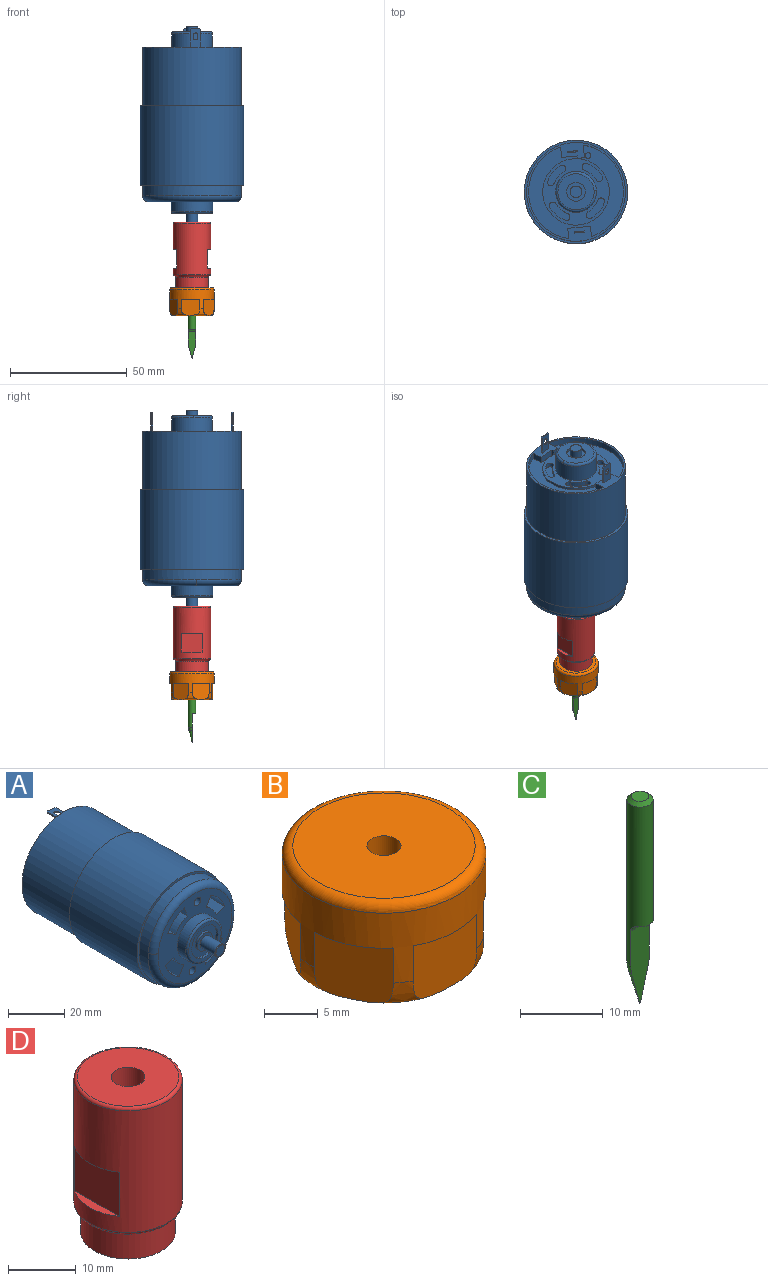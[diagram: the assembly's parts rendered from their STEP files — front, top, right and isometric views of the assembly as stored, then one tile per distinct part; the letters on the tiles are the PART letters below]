
ASSEMBLY  parts=4 mates=3
PART A: 110 faces, bbox 45.6x88x45.6 mm
  f0: torus R=18.65mm, axis (0,1,0), area 249.7mm2, adj f6,f28,f41
  f1: torus R=8.15mm, axis (0,1,0), area 31.9mm2, adj f8,f79,f85
  f2: torus R=7.75mm, axis (0,-1,0), area 41.4mm2, adj f19,f102,f104
  f3: torus R=2.25mm, axis (0,1,0), area 3mm2, adj f23,f107,f109
  f4: cylinder r=22.15mm len=44.3mm, axis (0,1,0), area 4731.9mm2, adj f25,f26
  f5: cylinder r=21.15mm len=42.3mm, axis (0,-1,0), area 3322.2mm2, adj f25,f27
  f6: cylinder r=21.15mm len=42.3mm, axis (0,-1,0), area 611.3mm2, adj f0,f26,f28
  f7: cylinder r=20.3mm len=39.26mm, axis (0,1,0), area 151mm2, adj f27,f31,f38,f51
  f8: cylinder r=8.9mm len=17.8mm, axis (0,-1,0), area 237.7mm2, adj f1,f41,f79
  f9: cylinder r=1.65mm len=11.5mm, axis (0,-1,0), area 119.2mm2, adj f13,f41
  f10: cylinder r=1.65mm len=11.5mm, axis (0,-1,0), area 119.2mm2, adj f14,f41
  f11: cylinder r=14.25mm len=28.5mm, axis (0,1,0), area 89.5mm2, adj f51,f83
  f12: cylinder r=1.25mm len=2.5mm, axis (0,1,0), area 0.8mm2, adj f51,f84
  f13: cone r=1.65mm half-angle=59deg, axis (0,-1,0), area 10mm2, adj f9
  f14: cone r=1.65mm half-angle=59deg, axis (0,-1,0), area 10mm2, adj f10
  f15: cylinder r=1.5mm len=2.9mm, axis (0,1,0), area 9.4mm2, adj f83,f86,f87,f98
  f16: cylinder r=1.5mm len=2.9mm, axis (0,1,0), area 9.4mm2, adj f83,f89,f90,f99
  f17: cylinder r=1.5mm len=2.79mm, axis (0,1,0), area 9.4mm2, adj f83,f92,f94,f100
  f18: cylinder r=1.5mm len=2.79mm, axis (0,1,0), area 9.4mm2, adj f83,f95,f97,f101
  f19: cylinder r=8.75mm len=17.5mm, axis (0,-1,0), area 412.3mm2, adj f2,f83,f102
  f20: cylinder r=6.62mm len=13.25mm, axis (0,-1,0), area 41.6mm2, adj f85,f103
  f21: cylinder r=3.75mm len=7.5mm, axis (0,-1,0), area 23.6mm2, adj f103,f105
  f22: cylinder r=4mm len=8mm, axis (0,1,0), area 25.1mm2, adj f104,f106
  f23: cylinder r=2.5mm len=7.55mm, axis (0,-1,0), area 118.6mm2, adj f3,f105,f107
  f24: cylinder r=2.5mm len=5mm, axis (0,-1,0), area 53.4mm2, adj f106,f108
  f25: plane 44.3x44.3mm, normal (0,1,0), area 136mm2, adj f4,f5
  f26: plane 44.3x44.3mm, normal (0,-1,0), area 136mm2, adj f4,f6
  f27: plane 42.3x42.3mm, normal (0,1,0), area 203.5mm2, adj f5,f7,f29,f30,f31,f32,f33,f34
  f28: torus R=18.65mm, axis (0,1,0), area 249.7mm2, adj f0,f6,f41
  f29: plane 8.15x4.58mm, normal (0.09,0,1), area 32.1mm2, adj f27,f42,f43,f44,f45,f46,f47,f48
  f30: plane 8.15x4.58mm, normal (-0.09,0,-1), area 32.1mm2, adj f27,f42,f43,f44,f45,f46,f47,f48
  f31: plane 4.44x2.8mm, normal (1,0,-0.09), area 12.5mm2, adj f7,f27,f32,f51
  f32: plane 9.71x2.8mm, normal (-0.09,0,-1), area 27.3mm2, adj f27,f31,f33,f51
  f33: plane 4.44x2.8mm, normal (-1,0,0.09), area 12.5mm2, adj f27,f32,f34,f51
  f34: cylinder r=20.3mm len=39.26mm, axis (0,1,0), area 151mm2, adj f27,f33,f35,f51
  f35: plane 4.44x2.8mm, normal (-1,0,0.09), area 12.5mm2, adj f27,f34,f36,f51
  f36: plane 6.92x2.8mm, normal (0.09,0,1), area 19.4mm2, adj f27,f35,f51,f52
  f37: plane 2.8x2.8mm, normal (0.09,0,1), area 7.9mm2, adj f27,f38,f51,f52
  f38: plane 5.44x2.8mm, normal (1,0,-0.09), area 15.3mm2, adj f7,f27,f37,f51
  f39: plane 8.15x4.58mm, normal (-0.09,0,-1), area 32.1mm2, adj f27,f53,f54,f55,f56,f57,f58,f59
  f40: plane 8.15x4.58mm, normal (0.09,0,1), area 32.1mm2, adj f27,f53,f54,f55,f56,f57,f58,f59
  f41: plane 37.3x37.3mm, normal (0,-1,0), area 647.6mm2, adj f0,f8,f9,f10,f28,f62,f63,f64
  f42: plane 3.63x0.81mm, normal (0,1,0), area 1.8mm2, adj f29,f30,f43,f46
  f43: plane 0.54x0.54mm, normal (-0.7,0.71,0.06), area 0.4mm2, adj f29,f30,f42,f44
  f44: plane 7.65x0.5mm, normal (-1,0,0.09), area 3.8mm2, adj f27,f29,f30,f43
  f45: plane 7.65x0.5mm, normal (1,0,-0.09), area 3.8mm2, adj f27,f29,f30,f46
  f46: plane 0.54x0.54mm, normal (0.7,0.71,-0.06), area 0.4mm2, adj f29,f30,f42,f45
  f47: plane 1x0.5mm, normal (1,0,-0.09), area 0.5mm2, adj f29,f30,f48,f50
  f48: cylinder r=1mm len=2.04mm, axis (0.09,0,1), area 1.6mm2, adj f29,f30,f47,f49
  f49: plane 1x0.5mm, normal (-1,0,0.09), area 0.5mm2, adj f29,f30,f48,f50
  f50: cylinder r=1mm len=2.04mm, axis (0.09,0,1), area 1.6mm2, adj f29,f30,f47,f49
  f51: plane 40.6x40.11mm, normal (0,1,0), area 554.3mm2, adj f7,f11,f12,f31,f32,f33,f34,f35
  f52: plane 2.8x1mm, normal (-1,0,0.09), area 2.8mm2, adj f27,f36,f37,f51
  f53: plane 7.65x0.5mm, normal (-1,0,0.09), area 3.8mm2, adj f27,f39,f40,f54
  f54: plane 0.54x0.54mm, normal (-0.7,0.71,0.06), area 0.4mm2, adj f39,f40,f53,f55
  f55: plane 3.63x0.81mm, normal (0,1,0), area 1.8mm2, adj f39,f40,f54,f56
  f56: plane 0.54x0.54mm, normal (0.7,0.71,-0.06), area 0.4mm2, adj f39,f40,f55,f57
  f57: plane 7.65x0.5mm, normal (1,0,-0.09), area 3.8mm2, adj f27,f39,f40,f56
  f58: plane 1x0.5mm, normal (-1,0,0.09), area 0.5mm2, adj f39,f40,f59,f61
  f59: cylinder r=1mm len=2.04mm, axis (-0.09,0,-1), area 1.6mm2, adj f39,f40,f58,f60
  f60: plane 1x0.5mm, normal (1,0,-0.09), area 0.5mm2, adj f39,f40,f59,f61
  f61: cylinder r=1mm len=2.04mm, axis (-0.09,0,-1), area 1.6mm2, adj f39,f40,f58,f60
  f62: plane 10x4.42mm, normal (-0.94,0,-0.34), area 47mm2, adj f41,f63,f65,f78
  f63: cylinder r=11.3mm len=10mm, axis (0,-1,0), area 78.9mm2, adj f41,f62,f64,f78
  f64: plane 10x4.07mm, normal (0.5,0,0.87), area 47mm2, adj f41,f63,f65,f78
  f65: cylinder r=16mm len=10mm, axis (0,-1,0), area 111.7mm2, adj f41,f62,f64,f78
  f66: cylinder r=16mm len=10mm, axis (0,-1,0), area 111.7mm2, adj f41,f67,f69,f80
  f67: plane 10x4.42mm, normal (0.94,0,0.34), area 47mm2, adj f41,f66,f68,f80
  f68: cylinder r=11.3mm len=10mm, axis (0,-1,0), area 78.9mm2, adj f41,f67,f69,f80
  f69: plane 10x4.07mm, normal (-0.5,0,-0.87), area 47mm2, adj f41,f66,f68,f80
  f70: plane 10x4.42mm, normal (-0.34,0,0.94), area 47mm2, adj f41,f71,f73,f81
  f71: cylinder r=11.3mm len=10mm, axis (0,-1,0), area 78.9mm2, adj f41,f70,f72,f81
  f72: plane 10x4.07mm, normal (0.87,0,-0.5), area 47mm2, adj f41,f71,f73,f81
  f73: cylinder r=16mm len=10mm, axis (0,-1,0), area 111.7mm2, adj f41,f70,f72,f81
  f74: cylinder r=16mm len=10mm, axis (0,-1,0), area 111.7mm2, adj f41,f75,f77,f82
  f75: plane 10x4.42mm, normal (0.34,0,-0.94), area 47mm2, adj f41,f74,f76,f82
  f76: cylinder r=11.3mm len=10mm, axis (0,-1,0), area 78.9mm2, adj f41,f75,f77,f82
  f77: plane 10x4.07mm, normal (-0.87,0,0.5), area 47mm2, adj f41,f74,f76,f82
  f78: plane 9.99x9.39mm, normal (0,-1,0), area 44.8mm2, adj f62,f63,f64,f65
  f79: torus R=8.15mm, axis (0,1,0), area 31.9mm2, adj f1,f8,f85
  f80: plane 9.99x9.39mm, normal (0,-1,0), area 44.8mm2, adj f66,f67,f68,f69
  f81: plane 9.99x9.39mm, normal (0,-1,0), area 44.8mm2, adj f70,f71,f72,f73
  f82: plane 9.99x9.39mm, normal (0,-1,0), area 44.8mm2, adj f74,f75,f76,f77
  f83: plane 28.5x28.5mm, normal (0,1,0), area 276.5mm2, adj f11,f15,f16,f17,f18,f19,f86,f87
  f84: plane 2.5x2.5mm, normal (0,1,0), area 4.9mm2, adj f12
  f85: plane 16.3x16.3mm, normal (0,-1,0), area 70.8mm2, adj f1,f20,f79
  f86: cylinder r=13mm len=6.56mm, axis (0,1,0), area 17.5mm2, adj f15,f83,f88,f98
  f87: cylinder r=10mm len=5.05mm, axis (0,1,0), area 13.4mm2, adj f15,f83,f88,f98
  f88: cylinder r=1.5mm len=2.79mm, axis (0,1,0), area 9.4mm2, adj f83,f86,f87,f98
  f89: cylinder r=13mm len=6.56mm, axis (0,1,0), area 17.5mm2, adj f16,f83,f91,f99
  f90: cylinder r=10mm len=5.05mm, axis (0,1,0), area 13.4mm2, adj f16,f83,f91,f99
  f91: cylinder r=1.5mm len=2.79mm, axis (0,1,0), area 9.4mm2, adj f83,f89,f90,f99
  f92: cylinder r=13mm len=6.56mm, axis (0,1,0), area 17.5mm2, adj f17,f83,f93,f100
  f93: cylinder r=1.5mm len=2.9mm, axis (0,1,0), area 9.4mm2, adj f83,f92,f94,f100
  f94: cylinder r=10mm len=5.05mm, axis (0,1,0), area 13.4mm2, adj f17,f83,f93,f100
  f95: cylinder r=13mm len=6.56mm, axis (0,1,0), area 17.5mm2, adj f18,f83,f96,f101
  f96: cylinder r=1.5mm len=2.9mm, axis (0,1,0), area 9.4mm2, adj f83,f95,f97,f101
  f97: cylinder r=10mm len=5.05mm, axis (0,1,0), area 13.4mm2, adj f18,f83,f96,f101
  f98: plane 8.8x7.87mm, normal (0,1,0), area 30.2mm2, adj f15,f86,f87,f88
  f99: plane 8.8x7.87mm, normal (0,1,0), area 30.2mm2, adj f16,f89,f90,f91
  f100: plane 8.8x7.87mm, normal (0,1,0), area 30.2mm2, adj f17,f92,f93,f94
  f101: plane 8.8x7.87mm, normal (0,1,0), area 30.2mm2, adj f18,f95,f96,f97
  f102: torus R=7.75mm, axis (0,-1,0), area 41.4mm2, adj f2,f19,f104
  f103: plane 13.25x13.25mm, normal (0,-1,0), area 93.7mm2, adj f20,f21
  f104: plane 15.5x15.5mm, normal (0,1,0), area 138.4mm2, adj f2,f22,f102
  f105: plane 7.5x7.5mm, normal (0,-1,0), area 24.5mm2, adj f21,f23
  f106: plane 8x8mm, normal (0,1,0), area 30.6mm2, adj f22,f24
  f107: torus R=2.25mm, axis (0,1,0), area 3mm2, adj f3,f23,f109
  f108: plane 5x5mm, normal (0,1,0), area 19.6mm2, adj f24
  f109: plane 4.5x4.5mm, normal (0,-1,0), area 15.9mm2, adj f3,f107
PART B: 19 faces, bbox 20.6x20.6x12 mm
  f0: cylinder r=9.5mm len=19mm, axis (0,0,1), area 284.4mm2, adj f3,f4,f5,f6,f7,f8,f9,f10
  f1: plane 17x17mm, normal (0,0,1), area 219.1mm2, adj f2,f15
  f2: cylinder r=1.59mm len=11.5mm, axis (0,0,-1), area 114.7mm2, adj f1,f18
  f3: plane 7.02x3.42mm, normal (0,0,-1), area 4.4mm2, adj f0,f4
  f4: plane 7.02x6.8mm, normal (-0.9,-0.44,0), area 50.7mm2, adj f0,f3,f16
  f5: plane 7.79x1.14mm, normal (0,0,-1), area 4.4mm2, adj f0,f6
  f6: plane 7.79x6.79mm, normal (-0.07,-1,0), area 50.8mm2, adj f0,f5,f16
  f7: plane 6.47x4.37mm, normal (0,0,-1), area 4.4mm2, adj f0,f8
  f8: plane 6.79x6.48mm, normal (0.83,-0.56,0), area 50.7mm2, adj f0,f7,f16
  f9: plane 7.02x3.42mm, normal (0,0,-1), area 4.4mm2, adj f0,f10
  f10: plane 7.02x6.8mm, normal (0.9,0.44,0), area 50.7mm2, adj f0,f9,f16
  f11: plane 7.79x1.14mm, normal (0,0,-1), area 4.4mm2, adj f0,f12
  f12: plane 7.79x6.79mm, normal (0.07,1,0), area 50.8mm2, adj f0,f11,f16
  f13: plane 6.47x4.37mm, normal (0,0,-1), area 4.4mm2, adj f0,f14
  f14: plane 6.79x6.48mm, normal (-0.83,0.56,0), area 50.7mm2, adj f0,f13,f16
  f15: torus R=8.5mm, axis (0,0,-1), area 90.2mm2, adj f0,f1
  f16: bspline ~18.97x18.97mm, area 156.6mm2, adj f0,f4,f6,f8,f10,f12,f14,f17
  f17: extruded ~12.93x12.93mm, area 20.4mm2, adj f16,f18
  f18: plane 13.1x13.1mm, normal (0,0,-1), area 124.7mm2, adj f2,f17
PART C: 9 faces, bbox 3.2x3.2x30.6 mm
  f0: cylinder r=1.59mm len=23.84mm, axis (0,0,-1), area 207.9mm2, adj f3,f5,f6,f7,f8
  f1: cone r=1.59mm half-angle=15deg, axis (0,0,1), area 12.1mm2, adj f2,f3,f7
  f2: sphere r=0.1mm, area 0mm2, adj f1,f7
  f3: revolved ~3.18x1.59mm, area 6.3mm2, adj f0,f1,f7
  f4: plane 2.18x2.18mm, normal (0,0,1), area 3.7mm2, adj f8
  f5: cylinder r=1mm len=3.18mm, axis (1,0,0), area 4.7mm2, adj f0,f6,f7
  f6: plane 2.47x0.59mm, normal (0,0,-1), area 1mm2, adj f0,f5
  f7: plane 11.38x3.18mm, normal (0,-1,0), area 27.6mm2, adj f0,f1,f2,f3,f5
  f8: cone r=1.09mm half-angle=45deg, axis (0,0,-1), area 5.9mm2, adj f0,f4
PART D: 16 faces, bbox 17.3x17.3x28 mm
  f0: cylinder r=1.59mm len=3.18mm, axis (0,0,-1), area 29.9mm2, adj f4,f5
  f1: cylinder r=8mm len=22mm, axis (0,0,-1), area 946.5mm2, adj f8,f9,f10,f11,f12,f13,f14,f15
  f2: plane 15x15mm, normal (0,0,1), area 157.1mm2, adj f6,f9
  f3: cylinder r=7mm len=14mm, axis (0,0,-1), area 197.9mm2, adj f4,f7
  f4: plane 14x14mm, normal (0,0,-1), area 146mm2, adj f0,f3
  f5: plane 5x5mm, normal (0,0,1), area 11.7mm2, adj f0,f6
  f6: cylinder r=2.5mm len=25mm, axis (0,0,1), area 392.7mm2, adj f2,f5
  f7: torus R=7.5mm, axis (0,0,1), area 35.4mm2, adj f3,f8
  f8: torus R=7.5mm, axis (0,0,1), area 38.6mm2, adj f1,f7
  f9: torus R=7.5mm, axis (0,0,1), area 38.6mm2, adj f1,f2
  f10: plane 9.33x1.5mm, normal (0,0,-1), area 9.5mm2, adj f1,f12
  f11: plane 9.33x1.5mm, normal (0,0,1), area 9.5mm2, adj f1,f12
  f12: plane 9.33x8mm, normal (-1,0,0), area 74.6mm2, adj f1,f10,f11
  f13: plane 9.33x1.5mm, normal (0,0,-1), area 9.5mm2, adj f1,f14
  f14: plane 9.33x8mm, normal (1,0,0), area 74.6mm2, adj f1,f13,f15
  f15: plane 9.33x1.5mm, normal (0,0,1), area 9.5mm2, adj f1,f14
PLACE A rot(axis=(1,0,0),90deg) t=(3.5,-61.08,49.98)mm
PLACE B t=(0,0,-23.97)mm
PLACE C t=(0,0,-48.47)mm
PLACE D t=(0,0,-23.97)mm
MATE fastened A.f102 <-> D.f0  axis (0,0,-1) through (0,0,4.03)mm
MATE fastened B.f0 <-> D.f0  axis (0,0,1) through (0,0,-23.97)mm
MATE fastened B.f0 <-> C.f0  axis (0,0,-1) through (0,0,-23.97)mm
